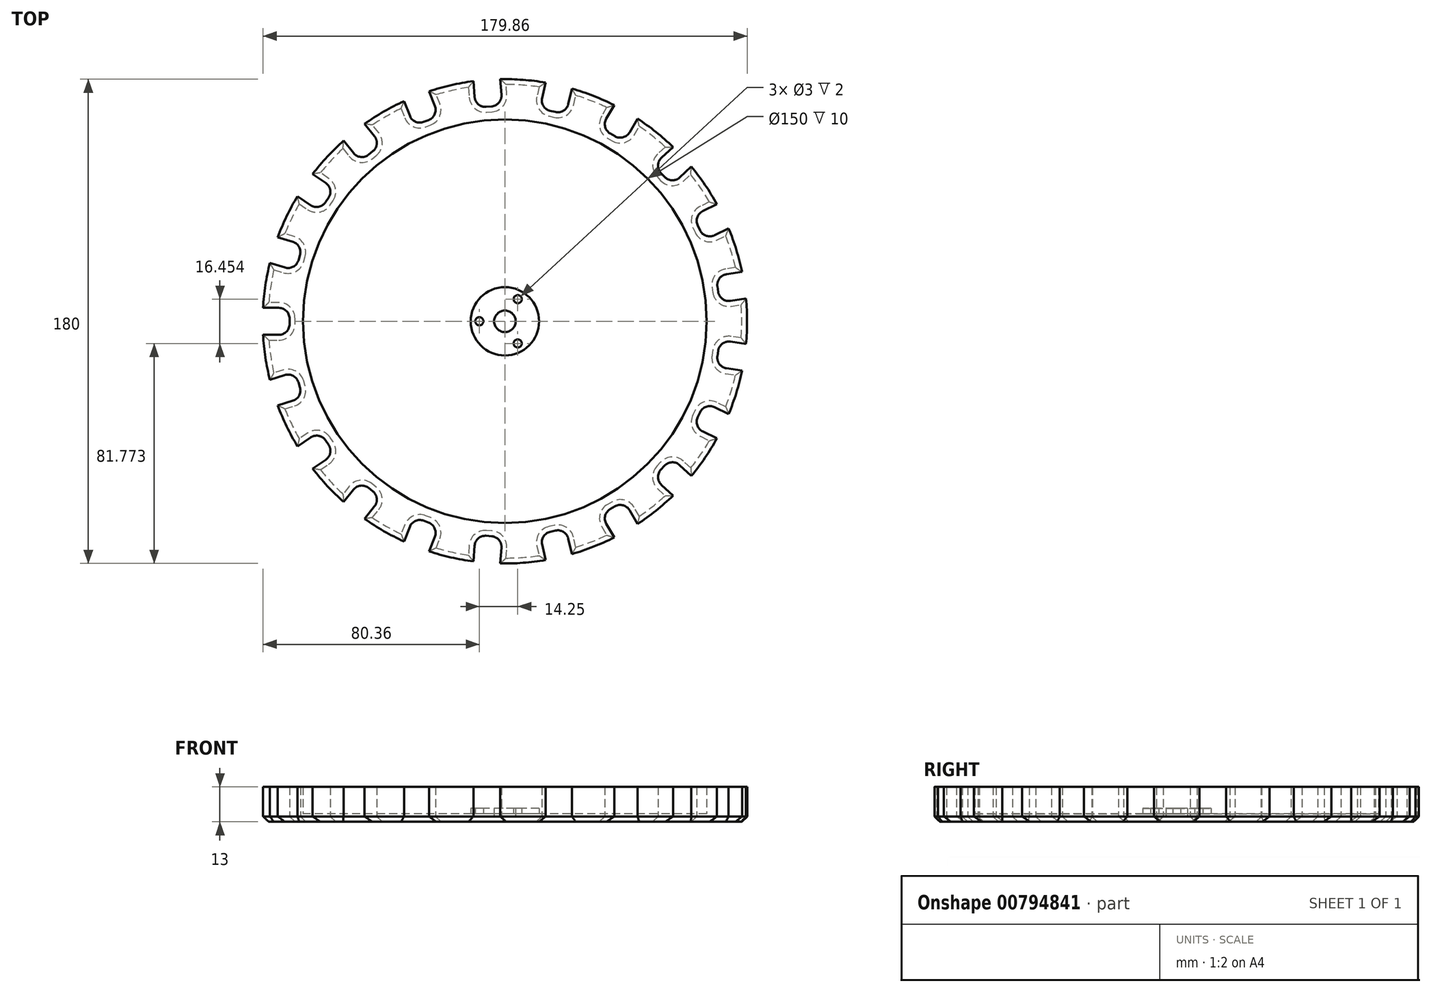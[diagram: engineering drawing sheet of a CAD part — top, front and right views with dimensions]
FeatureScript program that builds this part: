
annotation { "Feature Type Name" : "Feature", "Feature Type Description" : "" }
export const myFeature = defineFeature(function(context is Context, id is Id, definition is map)
    precondition{}
    {
        {
            var Q0;
            Q0=qCreatedBy(makeId("Top.planeOp"),FACE);
            var sketch = newSketch(context, id + "F0", { "sketchPlane" : qUnion([Q0])});
            skCircle(sketch, "E0", {"center": v(0, 0) * mm, "radius": 90 * mm});
            skCircle(sketch, "E1", {"center": v(0, 0) * mm, "radius": 75 * mm});
            skLineSegment(sketch, "E2", {"start": v(0, 0) * mm, "end": v(-124.02, 0) * mm, "construction": true});
            skPoint(sketch, "E3", {"position": v(-90, 0) * mm});
            skLineSegment(sketch, "E4.bottom", {"start": v(-90, -5) * mm, "end": v(-84, -5) * mm});
            skLineSegment(sketch, "E4.top", {"start": v(-90, 5) * mm, "end": v(-84, 5) * mm});
            skLineSegment(sketch, "E4.left", {"start": v(-90, -5) * mm, "end": v(-90, 5) * mm});
            skLineSegment(sketch, "E4.right", {"start": v(-80, -1) * mm, "end": v(-80, 1) * mm});
            skPoint(sketch, "E4.middle", {"position": v(-85, 0) * mm});
            skPoint(sketch, "E5.visualSharp", {"position": v(-80, 5) * mm});
            skArc(sketch, "E5.filletArc", {"start": v(-80, 1) * mm, "mid": v(-81.17, 3.83) * mm, "end": v(-84, 5) * mm});
            skPoint(sketch, "E6.visualSharp", {"position": v(-80, -5) * mm});
            skArc(sketch, "E6.filletArc", {"start": v(-84, -5) * mm, "mid": v(-81.17, -3.83) * mm, "end": v(-80, -1) * mm});
            skPoint(sketch, "E7.center", {"position": v(1.56, 0) * mm});
            skCircle(sketch, "E8", {"center": v(0, 0) * mm, "radius": 4 * mm});
            skCircle(sketch, "E9", {"center": v(0, 0) * mm, "radius": 12.7 * mm});
            skCircle(sketch, "E10", {"center": v(0, 0) * mm, "radius": 9.5 * mm, "construction": true});
            skCircle(sketch, "E11", {"center": v(-9.5, 0) * mm, "radius": 1.5 * mm});
            skCircle(sketch, "E12.1.0", {"center": v(-4.75, -8.23) * mm, "radius": 1.5 * mm});
            skCircle(sketch, "E12.2.0", {"center": v(4.75, -8.23) * mm, "radius": 1.5 * mm});
            skCircle(sketch, "E12.3.0", {"center": v(9.5, 0) * mm, "radius": 1.5 * mm});
            skCircle(sketch, "E12.4.0", {"center": v(4.75, 8.23) * mm, "radius": 1.5 * mm});
            skCircle(sketch, "E12.5.0", {"center": v(-4.75, 8.23) * mm, "radius": 1.5 * mm});
            skPoint(sketch, "E13.1.0", {"position": v(-77.92, -18.8) * mm});
            skPoint(sketch, "E13.1.1", {"position": v(-86, -26.53) * mm});
            skPoint(sketch, "E13.1.2", {"position": v(-74.97, -28.36) * mm});
            skPoint(sketch, "E13.1.3", {"position": v(-81.22, -25.05) * mm});
            skArc(sketch, "E13.1.4", {"start": v(-78.8, -29.54) * mm, "mid": v(-76.44, -27.58) * mm, "end": v(-76.15, -24.54) * mm});
            skArc(sketch, "E13.1.5", {"start": v(-76.74, -22.62) * mm, "mid": v(-78.7, -20.27) * mm, "end": v(-81.74, -19.98) * mm});
            skLineSegment(sketch, "E13.1.6", {"start": v(-84.53, -31.3) * mm, "end": v(-87.48, -21.75) * mm});
            skLineSegment(sketch, "E13.1.7", {"start": v(-76.15, -24.54) * mm, "end": v(-76.74, -22.62) * mm});
            skLineSegment(sketch, "E13.1.8", {"start": v(-87.48, -21.75) * mm, "end": v(-81.74, -19.98) * mm});
            skLineSegment(sketch, "E13.1.9", {"start": v(-84.53, -31.3) * mm, "end": v(-78.8, -29.54) * mm});
            skPoint(sketch, "E13.2.0", {"position": v(-68.92, -40.93) * mm});
            skPoint(sketch, "E13.2.1", {"position": v(-74.36, -50.7) * mm});
            skPoint(sketch, "E13.2.2", {"position": v(-63.28, -49.2) * mm});
            skPoint(sketch, "E13.2.3", {"position": v(-70.23, -47.88) * mm});
            skArc(sketch, "E13.2.4", {"start": v(-66.59, -51.45) * mm, "mid": v(-64.91, -48.89) * mm, "end": v(-65.54, -45.9) * mm});
            skArc(sketch, "E13.2.5", {"start": v(-66.66, -44.24) * mm, "mid": v(-69.22, -42.56) * mm, "end": v(-72.22, -43.19) * mm});
            skLineSegment(sketch, "E13.2.6", {"start": v(-71.54, -54.83) * mm, "end": v(-77.18, -46.57) * mm});
            skLineSegment(sketch, "E13.2.7", {"start": v(-65.54, -45.9) * mm, "end": v(-66.66, -44.24) * mm});
            skLineSegment(sketch, "E13.2.8", {"start": v(-77.18, -46.57) * mm, "end": v(-72.22, -43.19) * mm});
            skLineSegment(sketch, "E13.2.9", {"start": v(-71.54, -54.83) * mm, "end": v(-66.59, -51.45) * mm});
            skPoint(sketch, "E13.3.0", {"position": v(-53.79, -59.43) * mm});
            skPoint(sketch, "E13.3.1", {"position": v(-56.11, -70.36) * mm});
            skPoint(sketch, "E13.3.2", {"position": v(-45.97, -65.66) * mm});
            skPoint(sketch, "E13.3.3", {"position": v(-53, -66.46) * mm});
            skArc(sketch, "E13.3.4", {"start": v(-48.46, -68.8) * mm, "mid": v(-47.62, -65.85) * mm, "end": v(-49.1, -63.17) * mm});
            skArc(sketch, "E13.3.5", {"start": v(-50.66, -61.92) * mm, "mid": v(-53.6, -61.08) * mm, "end": v(-56.28, -62.56) * mm});
            skLineSegment(sketch, "E13.3.6", {"start": v(-52.2, -73.48) * mm, "end": v(-60.02, -67.25) * mm});
            skLineSegment(sketch, "E13.3.7", {"start": v(-49.1, -63.17) * mm, "end": v(-50.66, -61.92) * mm});
            skLineSegment(sketch, "E13.3.8", {"start": v(-60.02, -67.25) * mm, "end": v(-56.28, -62.56) * mm});
            skLineSegment(sketch, "E13.3.9", {"start": v(-52.2, -73.48) * mm, "end": v(-48.46, -68.8) * mm});
            skPoint(sketch, "E13.4.0", {"position": v(-33.88, -72.64) * mm});
            skPoint(sketch, "E13.4.1", {"position": v(-32.88, -83.78) * mm});
            skPoint(sketch, "E13.4.2", {"position": v(-24.57, -76.3) * mm});
            skPoint(sketch, "E13.4.3", {"position": v(-31.05, -79.12) * mm});
            skArc(sketch, "E13.4.4", {"start": v(-26.03, -80.02) * mm, "mid": v(-26.1, -76.96) * mm, "end": v(-28.3, -74.84) * mm});
            skArc(sketch, "E13.4.5", {"start": v(-30.16, -74.1) * mm, "mid": v(-33.22, -74.16) * mm, "end": v(-35.34, -76.37) * mm});
            skLineSegment(sketch, "E13.4.6", {"start": v(-28.23, -85.6) * mm, "end": v(-37.54, -81.95) * mm});
            skLineSegment(sketch, "E13.4.7", {"start": v(-28.3, -74.84) * mm, "end": v(-30.16, -74.1) * mm});
            skLineSegment(sketch, "E13.4.8", {"start": v(-37.54, -81.95) * mm, "end": v(-35.34, -76.37) * mm});
            skLineSegment(sketch, "E13.4.9", {"start": v(-28.23, -85.6) * mm, "end": v(-26.03, -80.02) * mm});
            skPoint(sketch, "E13.5.0", {"position": v(-10.96, -79.4) * mm});
            skPoint(sketch, "E13.5.1", {"position": v(-6.73, -89.75) * mm});
            skPoint(sketch, "E13.5.2", {"position": v(-1, -80.15) * mm});
            skPoint(sketch, "E13.5.3", {"position": v(-6.35, -84.76) * mm});
            skArc(sketch, "E13.5.4", {"start": v(-1.3, -84.14) * mm, "mid": v(-2.25, -81.23) * mm, "end": v(-4.98, -79.85) * mm});
            skArc(sketch, "E13.5.5", {"start": v(-6.98, -79.7) * mm, "mid": v(-9.88, -80.66) * mm, "end": v(-11.26, -83.4) * mm});
            skLineSegment(sketch, "E13.5.6", {"start": v(-1.74, -90.12) * mm, "end": v(-11.71, -89.37) * mm});
            skLineSegment(sketch, "E13.5.7", {"start": v(-4.98, -79.85) * mm, "end": v(-6.98, -79.7) * mm});
            skLineSegment(sketch, "E13.5.8", {"start": v(-11.71, -89.37) * mm, "end": v(-11.26, -83.4) * mm});
            skLineSegment(sketch, "E13.5.9", {"start": v(-1.74, -90.12) * mm, "end": v(-1.3, -84.14) * mm});
            skPoint(sketch, "E13.6.0", {"position": v(12.93, -79.1) * mm});
            skPoint(sketch, "E13.6.1", {"position": v(20.03, -87.74) * mm});
            skPoint(sketch, "E13.6.2", {"position": v(22.68, -76.88) * mm});
            skPoint(sketch, "E13.6.3", {"position": v(18.91, -82.87) * mm});
            skArc(sketch, "E13.6.4", {"start": v(23.57, -80.78) * mm, "mid": v(21.8, -78.28) * mm, "end": v(18.78, -77.77) * mm});
            skArc(sketch, "E13.6.5", {"start": v(16.83, -78.22) * mm, "mid": v(14.33, -79.99) * mm, "end": v(13.82, -83) * mm});
            skLineSegment(sketch, "E13.6.6", {"start": v(24.9, -86.63) * mm, "end": v(15.15, -88.86) * mm});
            skLineSegment(sketch, "E13.6.7", {"start": v(18.78, -77.77) * mm, "end": v(16.83, -78.22) * mm});
            skLineSegment(sketch, "E13.6.8", {"start": v(15.15, -88.86) * mm, "end": v(13.82, -83) * mm});
            skLineSegment(sketch, "E13.6.9", {"start": v(24.9, -86.63) * mm, "end": v(23.57, -80.78) * mm});
            skPoint(sketch, "E13.7.0", {"position": v(35.67, -71.78) * mm});
            skPoint(sketch, "E13.7.1", {"position": v(45, -77.94) * mm});
            skPoint(sketch, "E13.7.2", {"position": v(44.33, -66.78) * mm});
            skPoint(sketch, "E13.7.3", {"position": v(42.5, -73.61) * mm});
            skArc(sketch, "E13.7.4", {"start": v(46.33, -70.25) * mm, "mid": v(43.9, -68.38) * mm, "end": v(40.87, -68.78) * mm});
            skArc(sketch, "E13.7.5", {"start": v(39.13, -69.78) * mm, "mid": v(37.27, -72.21) * mm, "end": v(37.67, -75.25) * mm});
            skLineSegment(sketch, "E13.7.6", {"start": v(49.33, -75.44) * mm, "end": v(40.67, -80.44) * mm});
            skLineSegment(sketch, "E13.7.7", {"start": v(40.87, -68.78) * mm, "end": v(39.13, -69.78) * mm});
            skLineSegment(sketch, "E13.7.8", {"start": v(40.67, -80.44) * mm, "end": v(37.67, -75.25) * mm});
            skLineSegment(sketch, "E13.7.9", {"start": v(49.33, -75.44) * mm, "end": v(46.33, -70.25) * mm});
            skPoint(sketch, "E13.8.0", {"position": v(55.24, -58.08) * mm});
            skPoint(sketch, "E13.8.1", {"position": v(65.97, -61.22) * mm});
            skPoint(sketch, "E13.8.2", {"position": v(62.05, -50.75) * mm});
            skPoint(sketch, "E13.8.3", {"position": v(62.3, -57.81) * mm});
            skArc(sketch, "E13.8.4", {"start": v(64.98, -53.47) * mm, "mid": v(62.1, -52.4) * mm, "end": v(59.32, -53.68) * mm});
            skArc(sketch, "E13.8.5", {"start": v(57.96, -55.15) * mm, "mid": v(56.9, -58.02) * mm, "end": v(58.18, -60.8) * mm});
            skLineSegment(sketch, "E13.8.6", {"start": v(69.38, -57.55) * mm, "end": v(62.57, -64.88) * mm});
            skLineSegment(sketch, "E13.8.7", {"start": v(59.32, -53.68) * mm, "end": v(57.96, -55.15) * mm});
            skLineSegment(sketch, "E13.8.8", {"start": v(62.57, -64.88) * mm, "end": v(58.18, -60.8) * mm});
            skLineSegment(sketch, "E13.8.9", {"start": v(69.38, -57.55) * mm, "end": v(64.98, -53.47) * mm});
            skPoint(sketch, "E13.9.0", {"position": v(69.9, -39.22) * mm});
            skPoint(sketch, "E13.9.1", {"position": v(81.09, -39.05) * mm});
            skPoint(sketch, "E13.9.2", {"position": v(74.25, -30.2) * mm});
            skPoint(sketch, "E13.9.3", {"position": v(76.58, -36.88) * mm});
            skArc(sketch, "E13.9.4", {"start": v(77.85, -31.94) * mm, "mid": v(74.8, -31.77) * mm, "end": v(72.51, -33.8) * mm});
            skArc(sketch, "E13.9.5", {"start": v(71.64, -35.61) * mm, "mid": v(71.47, -38.67) * mm, "end": v(73.51, -40.95) * mm});
            skLineSegment(sketch, "E13.9.6", {"start": v(83.26, -34.54) * mm, "end": v(78.92, -43.55) * mm});
            skLineSegment(sketch, "E13.9.7", {"start": v(72.51, -33.8) * mm, "end": v(71.64, -35.61) * mm});
            skLineSegment(sketch, "E13.9.8", {"start": v(78.92, -43.55) * mm, "end": v(73.51, -40.95) * mm});
            skLineSegment(sketch, "E13.9.9", {"start": v(83.26, -34.54) * mm, "end": v(77.85, -31.94) * mm});
            skPoint(sketch, "E13.10.0", {"position": v(78.36, -16.87) * mm});
            skPoint(sketch, "E13.10.1", {"position": v(89, -13.41) * mm});
            skPoint(sketch, "E13.10.2", {"position": v(79.85, -6.98) * mm});
            skPoint(sketch, "E13.10.3", {"position": v(84.05, -12.67) * mm});
            skArc(sketch, "E13.10.4", {"start": v(83.8, -7.58) * mm, "mid": v(80.84, -8.31) * mm, "end": v(79.26, -10.93) * mm});
            skArc(sketch, "E13.10.5", {"start": v(78.96, -12.91) * mm, "mid": v(79.7, -15.88) * mm, "end": v(82.32, -17.46) * mm});
            skLineSegment(sketch, "E13.10.6", {"start": v(89.74, -8.47) * mm, "end": v(88.25, -18.36) * mm});
            skLineSegment(sketch, "E13.10.7", {"start": v(79.26, -10.93) * mm, "end": v(78.96, -12.91) * mm});
            skLineSegment(sketch, "E13.10.8", {"start": v(88.25, -18.36) * mm, "end": v(82.32, -17.46) * mm});
            skLineSegment(sketch, "E13.10.9", {"start": v(89.74, -8.47) * mm, "end": v(83.8, -7.58) * mm});
            skPoint(sketch, "E13.11.0", {"position": v(79.85, 6.98) * mm});
            skPoint(sketch, "E13.11.1", {"position": v(89, 13.41) * mm});
            skPoint(sketch, "E13.11.2", {"position": v(78.36, 16.87) * mm});
            skPoint(sketch, "E13.11.3", {"position": v(84.05, 12.67) * mm});
            skArc(sketch, "E13.11.4", {"start": v(82.32, 17.46) * mm, "mid": v(79.7, 15.88) * mm, "end": v(78.96, 12.91) * mm});
            skArc(sketch, "E13.11.5", {"start": v(79.26, 10.93) * mm, "mid": v(80.84, 8.31) * mm, "end": v(83.8, 7.58) * mm});
            skLineSegment(sketch, "E13.11.6", {"start": v(88.25, 18.36) * mm, "end": v(89.74, 8.47) * mm});
            skLineSegment(sketch, "E13.11.7", {"start": v(78.96, 12.91) * mm, "end": v(79.26, 10.93) * mm});
            skLineSegment(sketch, "E13.11.8", {"start": v(89.74, 8.47) * mm, "end": v(83.8, 7.58) * mm});
            skLineSegment(sketch, "E13.11.9", {"start": v(88.25, 18.36) * mm, "end": v(82.32, 17.46) * mm});
            skPoint(sketch, "E13.12.0", {"position": v(74.25, 30.2) * mm});
            skPoint(sketch, "E13.12.1", {"position": v(81.09, 39.05) * mm});
            skPoint(sketch, "E13.12.2", {"position": v(69.9, 39.22) * mm});
            skPoint(sketch, "E13.12.3", {"position": v(76.58, 36.88) * mm});
            skArc(sketch, "E13.12.4", {"start": v(73.51, 40.95) * mm, "mid": v(71.47, 38.67) * mm, "end": v(71.64, 35.61) * mm});
            skArc(sketch, "E13.12.5", {"start": v(72.51, 33.8) * mm, "mid": v(74.8, 31.77) * mm, "end": v(77.85, 31.94) * mm});
            skLineSegment(sketch, "E13.12.6", {"start": v(78.92, 43.55) * mm, "end": v(83.26, 34.54) * mm});
            skLineSegment(sketch, "E13.12.7", {"start": v(71.64, 35.61) * mm, "end": v(72.51, 33.8) * mm});
            skLineSegment(sketch, "E13.12.8", {"start": v(83.26, 34.54) * mm, "end": v(77.85, 31.94) * mm});
            skLineSegment(sketch, "E13.12.9", {"start": v(78.92, 43.55) * mm, "end": v(73.51, 40.95) * mm});
            skPoint(sketch, "E13.13.0", {"position": v(62.05, 50.75) * mm});
            skPoint(sketch, "E13.13.1", {"position": v(65.97, 61.22) * mm});
            skPoint(sketch, "E13.13.2", {"position": v(55.24, 58.08) * mm});
            skPoint(sketch, "E13.13.3", {"position": v(62.3, 57.81) * mm});
            skArc(sketch, "E13.13.4", {"start": v(58.18, 60.8) * mm, "mid": v(56.9, 58.02) * mm, "end": v(57.96, 55.15) * mm});
            skArc(sketch, "E13.13.5", {"start": v(59.32, 53.68) * mm, "mid": v(62.1, 52.4) * mm, "end": v(64.98, 53.47) * mm});
            skLineSegment(sketch, "E13.13.6", {"start": v(62.57, 64.88) * mm, "end": v(69.38, 57.55) * mm});
            skLineSegment(sketch, "E13.13.7", {"start": v(57.96, 55.15) * mm, "end": v(59.32, 53.68) * mm});
            skLineSegment(sketch, "E13.13.8", {"start": v(69.38, 57.55) * mm, "end": v(64.98, 53.47) * mm});
            skLineSegment(sketch, "E13.13.9", {"start": v(62.57, 64.88) * mm, "end": v(58.18, 60.8) * mm});
            skPoint(sketch, "E13.14.0", {"position": v(44.33, 66.78) * mm});
            skPoint(sketch, "E13.14.1", {"position": v(45, 77.94) * mm});
            skPoint(sketch, "E13.14.2", {"position": v(35.67, 71.78) * mm});
            skPoint(sketch, "E13.14.3", {"position": v(42.5, 73.61) * mm});
            skArc(sketch, "E13.14.4", {"start": v(37.67, 75.25) * mm, "mid": v(37.27, 72.21) * mm, "end": v(39.13, 69.78) * mm});
            skArc(sketch, "E13.14.5", {"start": v(40.87, 68.78) * mm, "mid": v(43.9, 68.38) * mm, "end": v(46.33, 70.25) * mm});
            skLineSegment(sketch, "E13.14.6", {"start": v(40.67, 80.44) * mm, "end": v(49.33, 75.44) * mm});
            skLineSegment(sketch, "E13.14.7", {"start": v(39.13, 69.78) * mm, "end": v(40.87, 68.78) * mm});
            skLineSegment(sketch, "E13.14.8", {"start": v(49.33, 75.44) * mm, "end": v(46.33, 70.25) * mm});
            skLineSegment(sketch, "E13.14.9", {"start": v(40.67, 80.44) * mm, "end": v(37.67, 75.25) * mm});
            skPoint(sketch, "E13.15.0", {"position": v(22.68, 76.88) * mm});
            skPoint(sketch, "E13.15.1", {"position": v(20.03, 87.74) * mm});
            skPoint(sketch, "E13.15.2", {"position": v(12.93, 79.1) * mm});
            skPoint(sketch, "E13.15.3", {"position": v(18.91, 82.87) * mm});
            skArc(sketch, "E13.15.4", {"start": v(13.82, 83) * mm, "mid": v(14.33, 79.99) * mm, "end": v(16.83, 78.22) * mm});
            skArc(sketch, "E13.15.5", {"start": v(18.78, 77.77) * mm, "mid": v(21.8, 78.28) * mm, "end": v(23.57, 80.78) * mm});
            skLineSegment(sketch, "E13.15.6", {"start": v(15.15, 88.86) * mm, "end": v(24.9, 86.63) * mm});
            skLineSegment(sketch, "E13.15.7", {"start": v(16.83, 78.22) * mm, "end": v(18.78, 77.77) * mm});
            skLineSegment(sketch, "E13.15.8", {"start": v(24.9, 86.63) * mm, "end": v(23.57, 80.78) * mm});
            skLineSegment(sketch, "E13.15.9", {"start": v(15.15, 88.86) * mm, "end": v(13.82, 83) * mm});
            skPoint(sketch, "E13.16.0", {"position": v(-1, 80.15) * mm});
            skPoint(sketch, "E13.16.1", {"position": v(-6.73, 89.75) * mm});
            skPoint(sketch, "E13.16.2", {"position": v(-10.96, 79.4) * mm});
            skPoint(sketch, "E13.16.3", {"position": v(-6.35, 84.76) * mm});
            skArc(sketch, "E13.16.4", {"start": v(-11.26, 83.4) * mm, "mid": v(-9.88, 80.66) * mm, "end": v(-6.98, 79.7) * mm});
            skArc(sketch, "E13.16.5", {"start": v(-4.98, 79.85) * mm, "mid": v(-2.25, 81.23) * mm, "end": v(-1.3, 84.14) * mm});
            skLineSegment(sketch, "E13.16.6", {"start": v(-11.71, 89.37) * mm, "end": v(-1.74, 90.12) * mm});
            skLineSegment(sketch, "E13.16.7", {"start": v(-6.98, 79.7) * mm, "end": v(-4.98, 79.85) * mm});
            skLineSegment(sketch, "E13.16.8", {"start": v(-1.74, 90.12) * mm, "end": v(-1.3, 84.14) * mm});
            skLineSegment(sketch, "E13.16.9", {"start": v(-11.71, 89.37) * mm, "end": v(-11.26, 83.4) * mm});
            skPoint(sketch, "E13.17.0", {"position": v(-24.57, 76.3) * mm});
            skPoint(sketch, "E13.17.1", {"position": v(-32.88, 83.78) * mm});
            skPoint(sketch, "E13.17.2", {"position": v(-33.88, 72.64) * mm});
            skPoint(sketch, "E13.17.3", {"position": v(-31.05, 79.12) * mm});
            skArc(sketch, "E13.17.4", {"start": v(-35.34, 76.37) * mm, "mid": v(-33.22, 74.16) * mm, "end": v(-30.16, 74.1) * mm});
            skArc(sketch, "E13.17.5", {"start": v(-28.3, 74.84) * mm, "mid": v(-26.1, 76.96) * mm, "end": v(-26.03, 80.02) * mm});
            skLineSegment(sketch, "E13.17.6", {"start": v(-37.54, 81.95) * mm, "end": v(-28.23, 85.6) * mm});
            skLineSegment(sketch, "E13.17.7", {"start": v(-30.16, 74.1) * mm, "end": v(-28.3, 74.84) * mm});
            skLineSegment(sketch, "E13.17.8", {"start": v(-28.23, 85.6) * mm, "end": v(-26.03, 80.02) * mm});
            skLineSegment(sketch, "E13.17.9", {"start": v(-37.54, 81.95) * mm, "end": v(-35.34, 76.37) * mm});
            skPoint(sketch, "E14.1.18.0", {"position": v(-56.11, 70.36) * mm});
            skPoint(sketch, "E14.2.18.0", {"position": v(-53.79, 59.43) * mm});
            skPoint(sketch, "E14.3.18.0", {"position": v(-53, 66.46) * mm});
            skArc(sketch, "E14.4.18.0", {"start": v(-56.28, 62.56) * mm, "mid": v(-53.6, 61.08) * mm, "end": v(-50.66, 61.92) * mm});
            skArc(sketch, "E14.8.18.0", {"start": v(-49.1, 63.17) * mm, "mid": v(-47.62, 65.85) * mm, "end": v(-48.46, 68.8) * mm});
            skLineSegment(sketch, "E14.12.18.0", {"start": v(-60.02, 67.25) * mm, "end": v(-52.2, 73.48) * mm});
            skPoint(sketch, "E14.13.18.0", {"position": v(-45.97, 65.66) * mm});
            skLineSegment(sketch, "E14.15.18.0", {"start": v(-50.66, 61.92) * mm, "end": v(-49.1, 63.17) * mm});
            skLineSegment(sketch, "E14.18.18.0", {"start": v(-52.2, 73.48) * mm, "end": v(-48.46, 68.8) * mm});
            skLineSegment(sketch, "E14.21.18.0", {"start": v(-60.02, 67.25) * mm, "end": v(-56.28, 62.56) * mm});
            skPoint(sketch, "E14.1.19.0", {"position": v(-74.36, 50.7) * mm});
            skPoint(sketch, "E14.2.19.0", {"position": v(-68.92, 40.93) * mm});
            skPoint(sketch, "E14.3.19.0", {"position": v(-70.23, 47.88) * mm});
            skArc(sketch, "E14.4.19.0", {"start": v(-72.22, 43.19) * mm, "mid": v(-69.22, 42.56) * mm, "end": v(-66.66, 44.24) * mm});
            skArc(sketch, "E14.8.19.0", {"start": v(-65.54, 45.9) * mm, "mid": v(-64.91, 48.89) * mm, "end": v(-66.59, 51.45) * mm});
            skLineSegment(sketch, "E14.12.19.0", {"start": v(-77.18, 46.57) * mm, "end": v(-71.54, 54.83) * mm});
            skPoint(sketch, "E14.13.19.0", {"position": v(-63.28, 49.2) * mm});
            skLineSegment(sketch, "E14.15.19.0", {"start": v(-66.66, 44.24) * mm, "end": v(-65.54, 45.9) * mm});
            skLineSegment(sketch, "E14.18.19.0", {"start": v(-71.54, 54.83) * mm, "end": v(-66.59, 51.45) * mm});
            skLineSegment(sketch, "E14.21.19.0", {"start": v(-77.18, 46.57) * mm, "end": v(-72.22, 43.19) * mm});
            skPoint(sketch, "E14.1.20.0", {"position": v(-86, 26.53) * mm});
            skPoint(sketch, "E14.2.20.0", {"position": v(-77.92, 18.8) * mm});
            skPoint(sketch, "E14.3.20.0", {"position": v(-81.22, 25.05) * mm});
            skArc(sketch, "E14.4.20.0", {"start": v(-81.74, 19.98) * mm, "mid": v(-78.7, 20.27) * mm, "end": v(-76.74, 22.62) * mm});
            skArc(sketch, "E14.8.20.0", {"start": v(-76.15, 24.54) * mm, "mid": v(-76.44, 27.58) * mm, "end": v(-78.8, 29.54) * mm});
            skLineSegment(sketch, "E14.12.20.0", {"start": v(-87.48, 21.75) * mm, "end": v(-84.53, 31.3) * mm});
            skPoint(sketch, "E14.13.20.0", {"position": v(-74.97, 28.36) * mm});
            skLineSegment(sketch, "E14.15.20.0", {"start": v(-76.74, 22.62) * mm, "end": v(-76.15, 24.54) * mm});
            skLineSegment(sketch, "E14.18.20.0", {"start": v(-84.53, 31.3) * mm, "end": v(-78.8, 29.54) * mm});
            skLineSegment(sketch, "E14.21.20.0", {"start": v(-87.48, 21.75) * mm, "end": v(-81.74, 19.98) * mm});
            skSolve(sketch);
        }
        {
            var Q0;
            Q0=makeQuery(id+"F0.imprint","IMPRINT",FACE,{"disambiguationData":[TD([[makeQuery(id+"F0.imprint","IMPRINT",EDGE,{"derivedFrom":sQuery(id+"F0.wireOp",EDGE,"E1")}),1.0]])]});
            var Q1;
            Q1=makeQuery(id+"F0.imprint","IMPRINT",FACE,{"disambiguationData":[TD([[makeQuery(id+"F0.imprint","IMPRINT",EDGE,{"derivedFrom":sQuery(id+"F0.wireOp",EDGE,"E8")}),-1.0]])]});
            var Q2;
            Q2=makeQuery(id+"F0.imprint","IMPRINT",FACE,{"disambiguationData":[TD([[makeQuery(id+"F0.imprint","IMPRINT",EDGE,{"derivedFrom":sQuery(id+"F0.wireOp",EDGE,"E12.3.0")}),1.0]])]});
            var Q3;
            Q3=makeQuery(id+"F0.imprint","IMPRINT",FACE,{"disambiguationData":[TD([[makeQuery(id+"F0.imprint","IMPRINT",EDGE,{"derivedFrom":sQuery(id+"F0.wireOp",EDGE,"E12.4.0")}),1.0]])]});
            var Q4;
            Q4=makeQuery(id+"F0.imprint","IMPRINT",FACE,{"disambiguationData":[TD([[makeQuery(id+"F0.imprint","IMPRINT",EDGE,{"derivedFrom":sQuery(id+"F0.wireOp",EDGE,"E12.5.0")}),1.0]])]});
            var Q5;
            Q5=makeQuery(id+"F0.imprint","IMPRINT",FACE,{"disambiguationData":[TD([[makeQuery(id+"F0.imprint","IMPRINT",EDGE,{"derivedFrom":sQuery(id+"F0.wireOp",EDGE,"E11")}),1.0]])]});
            var Q6;
            Q6=makeQuery(id+"F0.imprint","IMPRINT",FACE,{"disambiguationData":[TD([[makeQuery(id+"F0.imprint","IMPRINT",EDGE,{"derivedFrom":sQuery(id+"F0.wireOp",EDGE,"E12.1.0")}),1.0]])]});
            var Q7;
            Q7=makeQuery(id+"F0.imprint","IMPRINT",FACE,{"disambiguationData":[TD([[makeQuery(id+"F0.imprint","IMPRINT",EDGE,{"derivedFrom":sQuery(id+"F0.wireOp",EDGE,"E12.2.0")}),1.0]])]});
            extrude(context, id + "F1", {"entities" : qUnion([Q0, Q1, Q2, Q3, Q4, Q5, Q6, Q7]), "depth" : 3 * mm, "offsetDistance" : 25 * mm});
        }
        {
            var Q0;
            Q0=makeQuery(id+"F0.imprint","IMPRINT",FACE,{"disambiguationData":[TD([[makeQuery(id+"F0.imprint","IMPRINT",EDGE,{"derivedFrom":sQuery(id+"F0.wireOp",EDGE,"E1")}),-1.0]])]});
            extrude(context, id + "F2", {"entities" : qUnion([Q0]), "operationType" : NewBodyOperationType.ADD, "depth" : 13 * mm, "offsetDistance" : 25 * mm});
        }
        {
            var Q0;
            Q0=makeQuery(id+"F0.imprint","IMPRINT",FACE,{"disambiguationData":[TD([[makeQuery(id+"F0.imprint","IMPRINT",EDGE,{"derivedFrom":sQuery(id+"F0.wireOp",EDGE,"E8")}),-1.0]])]});
            var Q1;
            Q1=makeQuery(id+"F0.imprint","IMPRINT",FACE,{"disambiguationData":[TD([[makeQuery(id+"F0.imprint","IMPRINT",EDGE,{"derivedFrom":sQuery(id+"F0.wireOp",EDGE,"E12.5.0")}),1.0]])]});
            var Q2;
            Q2=makeQuery(id+"F0.imprint","IMPRINT",FACE,{"disambiguationData":[TD([[makeQuery(id+"F0.imprint","IMPRINT",EDGE,{"derivedFrom":sQuery(id+"F0.wireOp",EDGE,"E12.3.0")}),1.0]])]});
            var Q3;
            Q3=makeQuery(id+"F0.imprint","IMPRINT",FACE,{"disambiguationData":[TD([[makeQuery(id+"F0.imprint","IMPRINT",EDGE,{"derivedFrom":sQuery(id+"F0.wireOp",EDGE,"E12.1.0")}),1.0]])]});
            extrude(context, id + "F3", {"entities" : qUnion([Q0, Q1, Q2, Q3]), "operationType" : NewBodyOperationType.ADD, "depth" : 5 * mm, "offsetDistance" : 25 * mm});
        }
        {
            var Q0;
            Q0=makeQuery(id+"F0.imprint","IMPRINT",FACE,{"disambiguationData":[TD([[makeQuery(id+"F0.imprint","IMPRINT",EDGE,{"derivedFrom":sQuery(id+"F0.wireOp",EDGE,"E8")}),1.0]])]});
            extrude(context, id + "F4", {"entities" : qUnion([Q0]), "operationType" : NewBodyOperationType.ADD, "depth" : 2 * mm, "offsetDistance" : 25 * mm});
        }
        {
            var Q0;
            {var subQ0=sQuery(id+"F0.wireOp",EDGE,"E8");var subQ1=sQuery(id+"F0.wireOp",EDGE,"E1");Q0=makeQuery(id+"F4.boolean.opBoolean","MERGE",FACE,{"derivedFrom":[makeQuery(id+"F2.boolean.opBoolean","MERGE",FACE,{"derivedFrom":[makeQuery(id+"F1.opExtrude","CAP_FACE",FACE,{"disambiguationData":[OSD([subQ1,subQ0])],"isStart":true}),makeQuery(id+"F2.opExtrude","CAP_FACE",FACE,{"disambiguationData":[OSD([sQuery(id+"F0.wireOp",EDGE,"E0"),subQ1,sQuery(id+"F0.wireOp",EDGE,"E4.bottom"),sQuery(id+"F0.wireOp",EDGE,"E4.top"),sQuery(id+"F0.wireOp",EDGE,"E4.right"),sQuery(id+"F0.wireOp",EDGE,"E5.filletArc"),sQuery(id+"F0.wireOp",EDGE,"E6.filletArc"),sQuery(id+"F0.wireOp",EDGE,"E13.1.4"),sQuery(id+"F0.wireOp",EDGE,"E13.1.5"),sQuery(id+"F0.wireOp",EDGE,"E13.1.7"),sQuery(id+"F0.wireOp",EDGE,"E13.1.8"),sQuery(id+"F0.wireOp",EDGE,"E13.1.9"),sQuery(id+"F0.wireOp",EDGE,"E13.2.4"),sQuery(id+"F0.wireOp",EDGE,"E13.2.5"),sQuery(id+"F0.wireOp",EDGE,"E13.2.7"),sQuery(id+"F0.wireOp",EDGE,"E13.2.8"),sQuery(id+"F0.wireOp",EDGE,"E13.2.9"),sQuery(id+"F0.wireOp",EDGE,"E13.3.4"),sQuery(id+"F0.wireOp",EDGE,"E13.3.5"),sQuery(id+"F0.wireOp",EDGE,"E13.3.7"),sQuery(id+"F0.wireOp",EDGE,"E13.3.8"),sQuery(id+"F0.wireOp",EDGE,"E13.3.9"),sQuery(id+"F0.wireOp",EDGE,"E13.4.4"),sQuery(id+"F0.wireOp",EDGE,"E13.4.5"),sQuery(id+"F0.wireOp",EDGE,"E13.4.7"),sQuery(id+"F0.wireOp",EDGE,"E13.4.8"),sQuery(id+"F0.wireOp",EDGE,"E13.4.9"),sQuery(id+"F0.wireOp",EDGE,"E13.5.4"),sQuery(id+"F0.wireOp",EDGE,"E13.5.5"),sQuery(id+"F0.wireOp",EDGE,"E13.5.7"),sQuery(id+"F0.wireOp",EDGE,"E13.5.8"),sQuery(id+"F0.wireOp",EDGE,"E13.5.9"),sQuery(id+"F0.wireOp",EDGE,"E13.6.4"),sQuery(id+"F0.wireOp",EDGE,"E13.6.5"),sQuery(id+"F0.wireOp",EDGE,"E13.6.7"),sQuery(id+"F0.wireOp",EDGE,"E13.6.8"),sQuery(id+"F0.wireOp",EDGE,"E13.6.9"),sQuery(id+"F0.wireOp",EDGE,"E13.7.4"),sQuery(id+"F0.wireOp",EDGE,"E13.7.5"),sQuery(id+"F0.wireOp",EDGE,"E13.7.7"),sQuery(id+"F0.wireOp",EDGE,"E13.7.8"),sQuery(id+"F0.wireOp",EDGE,"E13.7.9"),sQuery(id+"F0.wireOp",EDGE,"E13.8.4"),sQuery(id+"F0.wireOp",EDGE,"E13.8.5"),sQuery(id+"F0.wireOp",EDGE,"E13.8.7"),sQuery(id+"F0.wireOp",EDGE,"E13.8.8"),sQuery(id+"F0.wireOp",EDGE,"E13.8.9"),sQuery(id+"F0.wireOp",EDGE,"E13.9.4"),sQuery(id+"F0.wireOp",EDGE,"E13.9.5"),sQuery(id+"F0.wireOp",EDGE,"E13.9.7"),sQuery(id+"F0.wireOp",EDGE,"E13.9.8"),sQuery(id+"F0.wireOp",EDGE,"E13.9.9"),sQuery(id+"F0.wireOp",EDGE,"E13.10.4"),sQuery(id+"F0.wireOp",EDGE,"E13.10.5"),sQuery(id+"F0.wireOp",EDGE,"E13.10.7"),sQuery(id+"F0.wireOp",EDGE,"E13.10.8"),sQuery(id+"F0.wireOp",EDGE,"E13.10.9"),sQuery(id+"F0.wireOp",EDGE,"E13.11.4"),sQuery(id+"F0.wireOp",EDGE,"E13.11.5"),sQuery(id+"F0.wireOp",EDGE,"E13.11.7"),sQuery(id+"F0.wireOp",EDGE,"E13.11.8"),sQuery(id+"F0.wireOp",EDGE,"E13.11.9"),sQuery(id+"F0.wireOp",EDGE,"E13.12.4"),sQuery(id+"F0.wireOp",EDGE,"E13.12.5"),sQuery(id+"F0.wireOp",EDGE,"E13.12.7"),sQuery(id+"F0.wireOp",EDGE,"E13.12.8"),sQuery(id+"F0.wireOp",EDGE,"E13.12.9"),sQuery(id+"F0.wireOp",EDGE,"E13.13.4"),sQuery(id+"F0.wireOp",EDGE,"E13.13.5"),sQuery(id+"F0.wireOp",EDGE,"E13.13.7"),sQuery(id+"F0.wireOp",EDGE,"E13.13.8"),sQuery(id+"F0.wireOp",EDGE,"E13.13.9"),sQuery(id+"F0.wireOp",EDGE,"E13.14.4"),sQuery(id+"F0.wireOp",EDGE,"E13.14.5"),sQuery(id+"F0.wireOp",EDGE,"E13.14.7"),sQuery(id+"F0.wireOp",EDGE,"E13.14.8"),sQuery(id+"F0.wireOp",EDGE,"E13.14.9"),sQuery(id+"F0.wireOp",EDGE,"E13.15.4"),sQuery(id+"F0.wireOp",EDGE,"E13.15.5"),sQuery(id+"F0.wireOp",EDGE,"E13.15.7"),sQuery(id+"F0.wireOp",EDGE,"E13.15.8"),sQuery(id+"F0.wireOp",EDGE,"E13.15.9"),sQuery(id+"F0.wireOp",EDGE,"E13.16.4"),sQuery(id+"F0.wireOp",EDGE,"E13.16.5"),sQuery(id+"F0.wireOp",EDGE,"E13.16.7"),sQuery(id+"F0.wireOp",EDGE,"E13.16.8"),sQuery(id+"F0.wireOp",EDGE,"E13.16.9"),sQuery(id+"F0.wireOp",EDGE,"E13.17.4"),sQuery(id+"F0.wireOp",EDGE,"E13.17.5"),sQuery(id+"F0.wireOp",EDGE,"E13.17.7"),sQuery(id+"F0.wireOp",EDGE,"E13.17.8"),sQuery(id+"F0.wireOp",EDGE,"E13.17.9")])],"isStart":true})]}),makeQuery(id+"F4.opExtrude","CAP_FACE",FACE,{"disambiguationData":[OSD([subQ0])],"isStart":true})]});}
            chamfer(context, id + "F5", {"entities" : qUnion([Q0]), "width" : 2 * mm, "tangentPropagation" : true});
        }
    });
